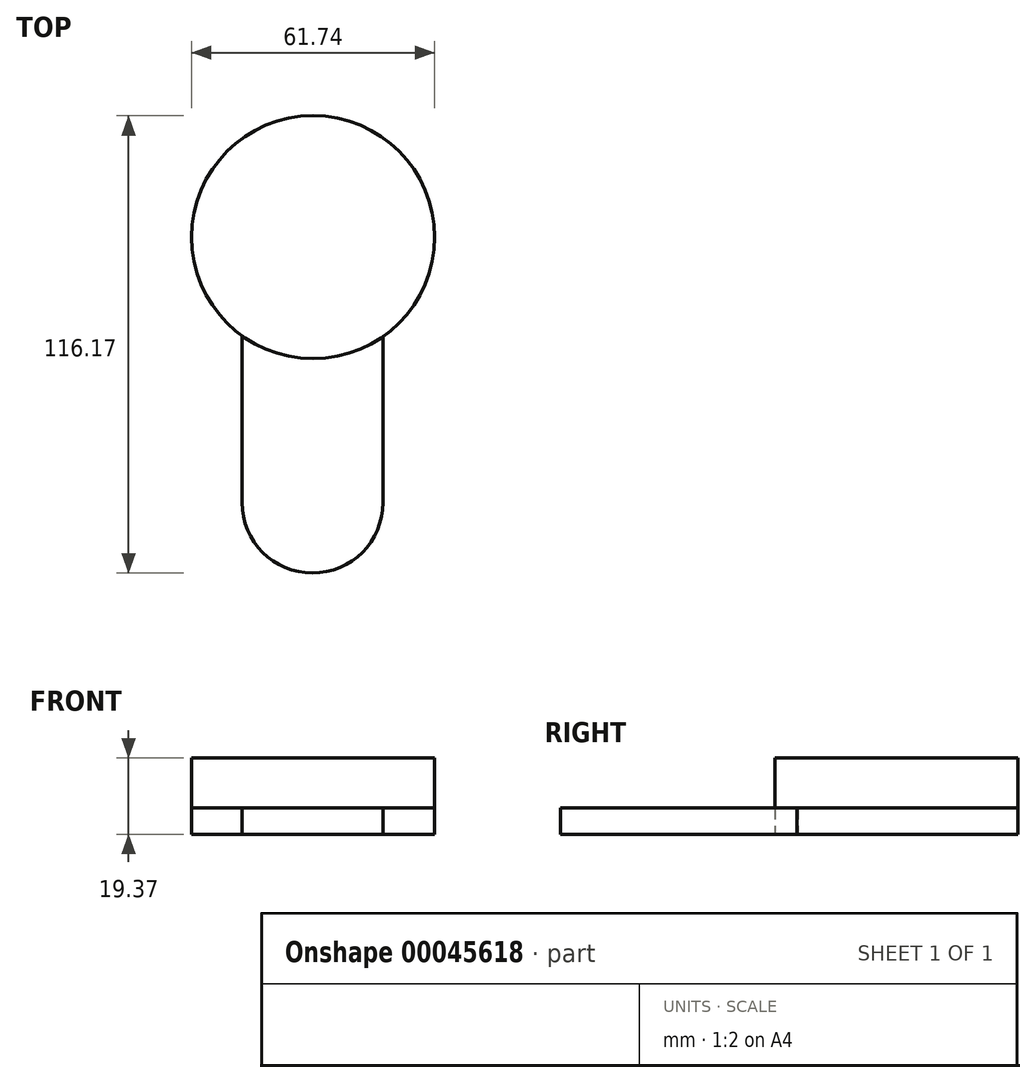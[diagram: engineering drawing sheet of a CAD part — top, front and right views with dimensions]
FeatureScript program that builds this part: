
annotation { "Feature Type Name" : "Feature", "Feature Type Description" : "" }
export const myFeature = defineFeature(function(context is Context, id is Id, definition is map)
    precondition{}
    {
        {
            var Q0;
            Q0=qCreatedBy(makeId("Top.planeOp"),FACE);
            var sketch = newSketch(context, id + "F0", { "sketchPlane" : qUnion([Q0])});
            skCircle(sketch, "E0", {"center": v(-22.6, 42.38) * mm, "radius": 30.87 * mm});
            skLineSegment(sketch, "E1", {"start": v(-4.86, 17.11) * mm, "end": v(-4.86, -25.03) * mm});
            skLineSegment(sketch, "E2", {"start": v(-40.64, 17.33) * mm, "end": v(-40.64, -25.03) * mm});
            skArc(sketch, "E3", {"start": v(-40.64, -25.03) * mm, "mid": v(-22.75, -42.92) * mm, "end": v(-4.86, -25.03) * mm});
            skSolve(sketch);
        }
        {
            var Q0;
            Q0=qCreatedBy(makeId("Top.planeOp"),FACE);
            var sketch = newSketch(context, id + "F1", { "sketchPlane" : qUnion([Q0])});
            skSolve(sketch);
        }
        {
            var Q0;
            Q0 = qSketchRegion(id + "F1", true);
            var Q1;
            {var subQ0=sQuery(id+"F0.wireOp",EDGE,"E0");var subQ2=makeQuery(id+"F0.imprint","INTERSECT",VERTEX,{"derivedFrom":[subQ0,sQuery(id+"F0.wireOp",EDGE,"E1")]});Q1=makeQuery(id+"F0.imprint","IMPRINT",FACE,{"disambiguationData":[TD([[makeQuery(id+"F0.imprint","IMPRINT",EDGE,{"disambiguationData":[TD([[subQ2,1.0]])],"derivedFrom":subQ0}),1.0]])]});}
            extrude(context, id + "F2", {"entities" : qUnion([Q0, Q1]), "depth" : 19.37 * mm});
        }
        {
            var Q0;
            Q0=qCreatedBy(makeId("Top.planeOp"),FACE);
            var sketch = newSketch(context, id + "F3", { "sketchPlane" : qUnion([Q0])});
            skLineSegment(sketch, "E4", {"start": v(-6.13, 16.14) * mm, "end": v(-6.13, -29.25) * mm});
            skLineSegment(sketch, "E5", {"start": v(-37.94, 16.14) * mm, "end": v(-37.94, -29.25) * mm});
            skArc(sketch, "E6", {"start": v(-37.94, -29.25) * mm, "mid": v(-22.03, -45.15) * mm, "end": v(-6.13, -29.25) * mm});
            skSolve(sketch);
        }
        {
            var Q0;
            Q0=sQuery(id+"F3.wireOp",EDGE,"E4");
            var Q1;
            Q1=sQuery(id+"F3.wireOp",EDGE,"E6");
            var Q2;
            Q2=sQuery(id+"F3.wireOp",EDGE,"E5");
            extrude(context, id + "F4", {"bodyType" : ToolBodyType.SURFACE, "surfaceEntities" : qUnion([Q0, Q1, Q2]), "depth" : 6.76 * mm});
        }
        {
            var Q0;
            Q0 = qSketchRegion(id + "F0", true);
            extrude(context, id + "F5", {"entities" : qUnion([Q0]), "depth" : 6.72 * mm});
        }
    });
